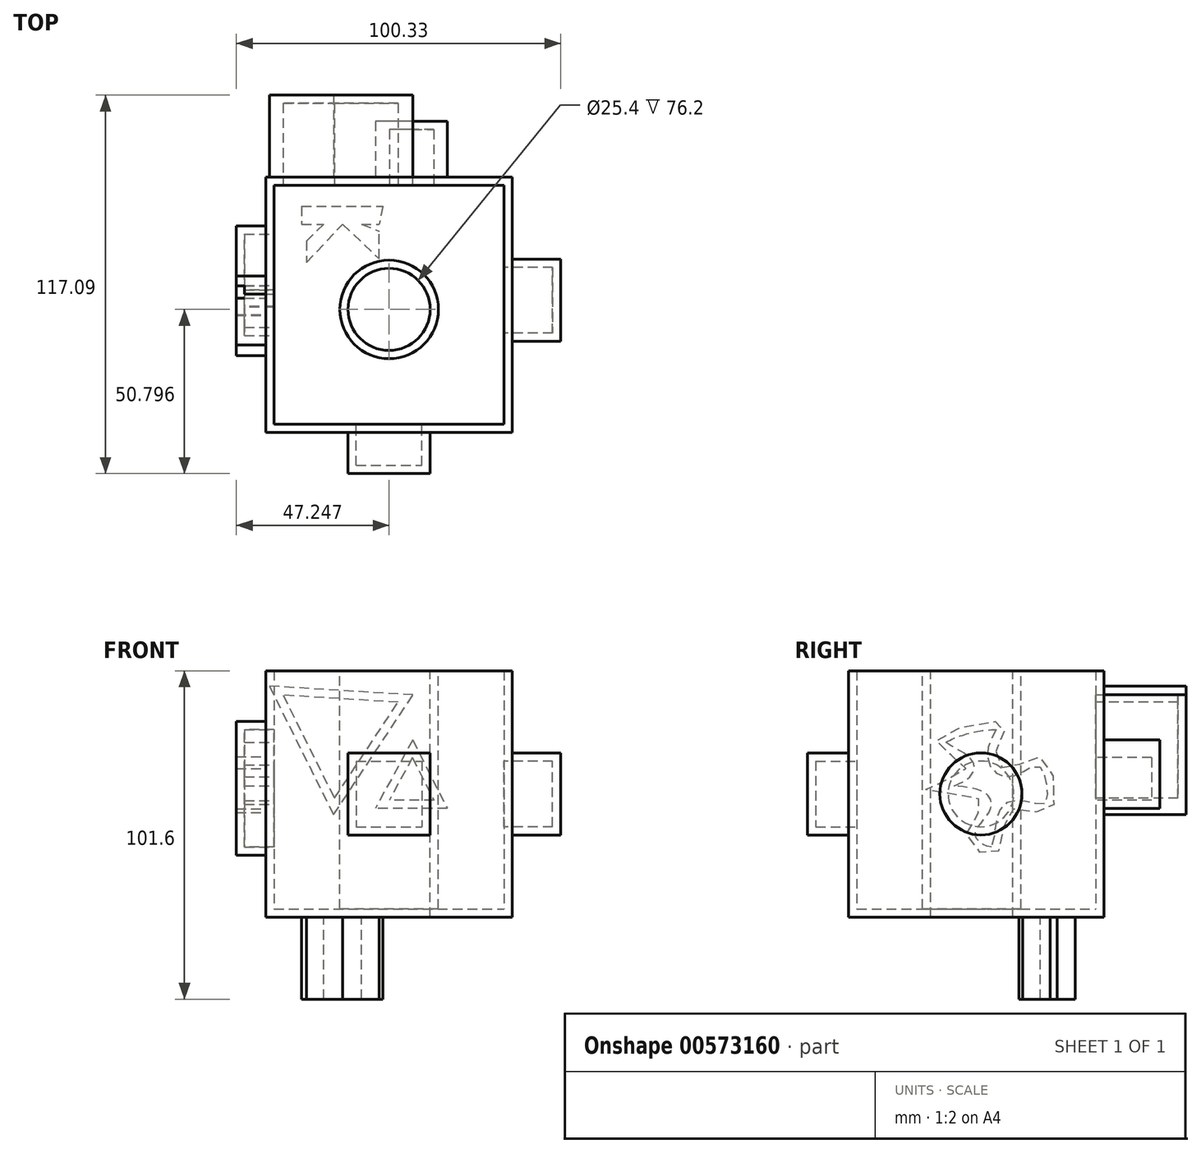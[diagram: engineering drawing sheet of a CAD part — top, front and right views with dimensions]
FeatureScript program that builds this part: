
annotation { "Feature Type Name" : "Feature", "Feature Type Description" : "" }
export const myFeature = defineFeature(function(context is Context, id is Id, definition is map)
    precondition{}
    {
        {
            var Q0;
            Q0=qCreatedBy(makeId("Front.planeOp"),FACE);
            var sketch = newSketch(context, id + "F0", { "sketchPlane" : qUnion([Q0])});
            skLineSegment(sketch, "E0.bottom", {"start": v(-88.37, 86.9) * mm, "end": v(-12.17, 86.9) * mm});
            skLineSegment(sketch, "E0.top", {"start": v(-88.37, 10.7) * mm, "end": v(-12.17, 10.7) * mm});
            skLineSegment(sketch, "E0.left", {"start": v(-88.37, 86.9) * mm, "end": v(-88.37, 10.7) * mm});
            skLineSegment(sketch, "E0.right", {"start": v(-12.17, 86.9) * mm, "end": v(-12.17, 10.7) * mm});
            skSolve(sketch);
        }
        {
            var Q0;
            Q0 = qSketchRegion(id + "F0", true);
            extrude(context, id + "F1", {"entities" : qUnion([Q0]), "depth" : 79 * mm, "offsetDistance" : 25.4 * mm});
        }
        {
            var Q0;
            Q0=makeQuery(id+"F1.opExtrude","CAP_FACE",FACE,{"disambiguationData":[OSD([sQuery(id+"F0.wireOp",EDGE,"E0.bottom"),sQuery(id+"F0.wireOp",EDGE,"E0.top"),sQuery(id+"F0.wireOp",EDGE,"E0.left"),sQuery(id+"F0.wireOp",EDGE,"E0.right")])],"isStart":false});
            var sketch = newSketch(context, id + "F2", { "sketchPlane" : qUnion([Q0])});
            skLineSegment(sketch, "E1.bottom", {"start": v(-62.97, 61.5) * mm, "end": v(-37.57, 61.5) * mm});
            skLineSegment(sketch, "E1.top", {"start": v(-62.97, 36.1) * mm, "end": v(-37.57, 36.1) * mm});
            skLineSegment(sketch, "E1.left", {"start": v(-62.97, 61.5) * mm, "end": v(-62.97, 36.1) * mm});
            skLineSegment(sketch, "E1.right", {"start": v(-37.57, 61.5) * mm, "end": v(-37.57, 36.1) * mm});
            skSolve(sketch);
        }
        {
            var Q0;
            Q0 = qSketchRegion(id + "F2", true);
            extrude(context, id + "F3", {"entities" : qUnion([Q0]), "operationType" : NewBodyOperationType.ADD, "depth" : 12.7 * mm, "offsetDistance" : 25.4 * mm});
        }
        {
            var Q0;
            Q0=makeQuery(id+"F1.opExtrude","SWEPT_FACE",FACE,{"disambiguationData":[OSD([sQuery(id+"F0.wireOp",EDGE,"E0.right")])]});
            var sketch = newSketch(context, id + "F4", { "sketchPlane" : qUnion([Q0])});
            skCircle(sketch, "E2", {"center": v(-38.1, 48.8) * mm, "radius": 12.7 * mm});
            skSolve(sketch);
        }
        {
            var Q0;
            Q0=makeQuery(id+"F1.opExtrude","SWEPT_FACE",FACE,{"disambiguationData":[OSD([sQuery(id+"F0.wireOp",EDGE,"E0.bottom")])]});
            var sketch = newSketch(context, id + "F5", { "sketchPlane" : qUnion([Q0])});
            skPoint(sketch, "E3", {"position": v(-50.27, -40.9) * mm});
            skSolve(sketch);
        }
        {
            var Q0;
            Q0=sQuery(id+"F5.wireOp",VERTEX,"E3");
            var Q1;
            Q1=makeQuery(id+"F1.opExtrude","SWEPT_BODY",BODY,{"disambiguationData":[OSD([sQuery(id+"F0.wireOp",EDGE,"E0.bottom"),sQuery(id+"F0.wireOp",EDGE,"E0.top"),sQuery(id+"F0.wireOp",EDGE,"E0.left"),sQuery(id+"F0.wireOp",EDGE,"E0.right")])]});
            hole(context, id + "F6", {"style" : HoleStyle.SIMPLE, "endStyle" : HoleEndStyle.THROUGH, "holeDiameter" : 25.4 * mm, "isTappedThrough" : true, "tappedDepth" : 12.7 * mm, "tapClearance" : 3, "locations" : qUnion([Q0]), "scope" : qUnion([Q1])});
        }
        {
            var Q0;
            Q0=makeQuery(id+"F4.imprint","IMPRINT",FACE,{"disambiguationData":[TD([[makeQuery(id+"F4.imprint","IMPRINT",EDGE,{"derivedFrom":sQuery(id+"F4.wireOp",EDGE,"E2")}),1.0]])]});
            extrude(context, id + "F7", {"entities" : qUnion([Q0]), "operationType" : NewBodyOperationType.ADD, "depth" : 15 * mm, "offsetDistance" : 25.4 * mm});
        }
        {
            var Q0;
            Q0=makeQuery(id+"F1.opExtrude","CAP_FACE",FACE,{"disambiguationData":[OSD([sQuery(id+"F0.wireOp",EDGE,"E0.bottom"),sQuery(id+"F0.wireOp",EDGE,"E0.top"),sQuery(id+"F0.wireOp",EDGE,"E0.left"),sQuery(id+"F0.wireOp",EDGE,"E0.right")])],"isStart":true});
            var sketch = newSketch(context, id + "F8", { "sketchPlane" : qUnion([Q0])});
            skLineSegment(sketch, "E4", {"start": v(43, 65.5) * mm, "end": v(32.28, 44.28) * mm});
            skLineSegment(sketch, "E5", {"start": v(43, 65.5) * mm, "end": v(54.5, 44.28) * mm});
            skLineSegment(sketch, "E6", {"start": v(32.28, 44.28) * mm, "end": v(54.5, 44.28) * mm});
            skSolve(sketch);
        }
        {
            var Q0;
            Q0=makeQuery(id+"F8.imprint","IMPRINT",FACE,{"disambiguationData":[TD([[makeQuery(id+"F8.imprint","IMPRINT",EDGE,{"derivedFrom":sQuery(id+"F8.wireOp",EDGE,"E4")}),1.0]])]});
            extrude(context, id + "F9", {"entities" : qUnion([Q0]), "operationType" : NewBodyOperationType.ADD, "depth" : 17.27 * mm, "offsetDistance" : 25.4 * mm});
        }
        {
            var Q0;
            Q0=makeQuery(id+"F1.opExtrude","SWEPT_FACE",FACE,{"disambiguationData":[OSD([sQuery(id+"F0.wireOp",EDGE,"E0.left")])]});
            var sketch = newSketch(context, id + "F10", { "sketchPlane" : qUnion([Q0])});
            skFitSpline(sketch, "E7", {"points": [v(33.51, 61.96) * mm, v(29.74, 56.59) * mm, v(19.15, 59.96) * mm, v(16.7, 43.75) * mm, v(29.2, 43.63) * mm, v(33.46, 30.25) * mm, v(42.51, 36.26) * mm, v(37.72, 46.55) * mm, v(55.23, 50.16) * mm, v(42.73, 56.85) * mm, v(51.93, 64.77) * mm, v(31.2, 70.66) * mm, v(33.51, 61.96) * mm]});
            skSolve(sketch);
        }
        {
            var Q0;
            Q0 = qSketchRegion(id + "F10", true);
            extrude(context, id + "F11", {"entities" : qUnion([Q0]), "operationType" : NewBodyOperationType.ADD, "depth" : 9.14 * mm, "offsetDistance" : 25.4 * mm});
        }
        {
            var Q0;
            Q0=makeQuery(id+"F1.opExtrude","CAP_FACE",FACE,{"disambiguationData":[OSD([sQuery(id+"F0.wireOp",EDGE,"E0.bottom"),sQuery(id+"F0.wireOp",EDGE,"E0.top"),sQuery(id+"F0.wireOp",EDGE,"E0.left"),sQuery(id+"F0.wireOp",EDGE,"E0.right")])],"isStart":true});
            var sketch = newSketch(context, id + "F12", { "sketchPlane" : qUnion([Q0])});
            skCircle(sketch, "E8.cCircle", {"center": v(65.9, 67.97) * mm, "radius": 12.84 * mm, "construction": true});
            skLineSegment(sketch, "E8.0", {"start": v(87.3, 82.15) * mm, "end": v(67.48, 42.34) * mm});
            skLineSegment(sketch, "E8.1", {"start": v(67.48, 42.34) * mm, "end": v(42.91, 79.41) * mm});
            skLineSegment(sketch, "E8.2", {"start": v(42.91, 79.41) * mm, "end": v(87.3, 82.15) * mm});
            skPoint(sketch, "E8.0.midPoint", {"position": v(77.39, 62.25) * mm});
            skSolve(sketch);
        }
        {
            var Q0;
            Q0=makeQuery(id+"F12.imprint","IMPRINT",FACE,{"disambiguationData":[TD([[makeQuery(id+"F12.imprint","IMPRINT",EDGE,{"derivedFrom":sQuery(id+"F12.wireOp",EDGE,"E8.0")}),-1.0]])]});
            extrude(context, id + "F13", {"entities" : qUnion([Q0]), "operationType" : NewBodyOperationType.ADD, "depth" : 25.4 * mm, "offsetDistance" : 25.4 * mm});
        }
        {
            var Q0;
            Q0=makeQuery(id+"F1.opExtrude","SWEPT_FACE",FACE,{"disambiguationData":[OSD([sQuery(id+"F0.wireOp",EDGE,"E0.bottom")])]});
            shell(context, id + "F14", {"entities" : qUnion([Q0]), "thickness" : 2.54 * mm});
        }
        {
            var Q0;
            Q0=makeQuery(id+"F1.opExtrude","SWEPT_FACE",FACE,{"disambiguationData":[OSD([sQuery(id+"F0.wireOp",EDGE,"E0.top")])]});
            var sketch = newSketch(context, id + "F15", { "sketchPlane" : qUnion([Q0])});
            skLineSegment(sketch, "E9", {"start": v(-77.3, 8.96) * mm, "end": v(-52.22, 8.96) * mm});
            skLineSegment(sketch, "E10", {"start": v(-77.3, 8.96) * mm, "end": v(-77.3, 14.53) * mm});
            skLineSegment(sketch, "E11", {"start": v(-77.3, 14.53) * mm, "end": v(-70.45, 14.53) * mm});
            skLineSegment(sketch, "E12", {"start": v(-70.45, 14.53) * mm, "end": v(-75.87, 19.72) * mm});
            skLineSegment(sketch, "E13", {"start": v(-75.87, 19.72) * mm, "end": v(-75.87, 26.38) * mm});
            skLineSegment(sketch, "E14", {"start": v(-75.87, 26.38) * mm, "end": v(-64.62, 14.53) * mm});
            skLineSegment(sketch, "E15", {"start": v(-64.62, 14.53) * mm, "end": v(-53.35, 25.23) * mm});
            skLineSegment(sketch, "E16", {"start": v(-53.35, 25.23) * mm, "end": v(-53.35, 16.7) * mm});
            skLineSegment(sketch, "E17", {"start": v(-58.83, 14.53) * mm, "end": v(-53.35, 16.7) * mm});
            skLineSegment(sketch, "E18", {"start": v(-58.83, 14.53) * mm, "end": v(-53.35, 14.53) * mm});
            skLineSegment(sketch, "E19", {"start": v(-52.22, 8.96) * mm, "end": v(-53.35, 14.53) * mm});
            skSolve(sketch);
        }
        {
            var Q0;
            Q0=makeQuery(id+"F15.imprint","IMPRINT",FACE,{"disambiguationData":[TD([[makeQuery(id+"F15.imprint","IMPRINT",EDGE,{"derivedFrom":sQuery(id+"F15.wireOp",EDGE,"E9")}),1.0]])]});
            extrude(context, id + "F16", {"entities" : qUnion([Q0]), "operationType" : NewBodyOperationType.ADD, "depth" : 25.4 * mm, "offsetDistance" : 25.4 * mm});
        }
    });
